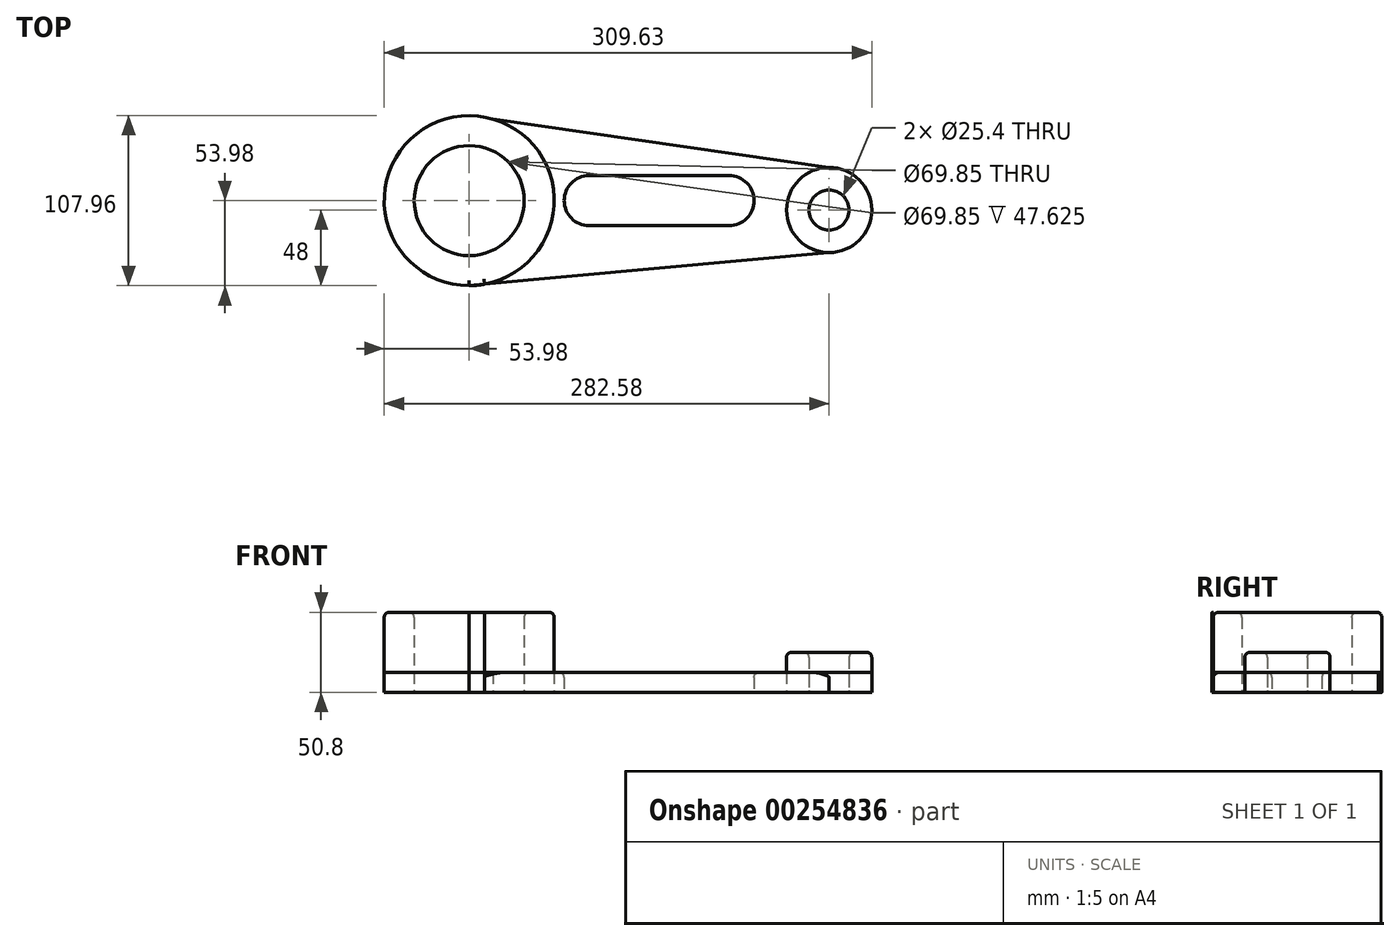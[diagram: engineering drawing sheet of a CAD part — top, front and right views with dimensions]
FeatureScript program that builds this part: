
annotation { "Feature Type Name" : "Feature", "Feature Type Description" : "" }
export const myFeature = defineFeature(function(context is Context, id is Id, definition is map)
    precondition{}
    {
        {
            var Q0;
            Q0=qCreatedBy(makeId("Top.planeOp"),FACE);
            var sketch = newSketch(context, id + "F0", { "sketchPlane" : qUnion([Q0])});
            skArc(sketch, "E0", {"start": v(0, -15.88) * mm, "mid": v(15.88, 0) * mm, "end": v(0, 15.88) * mm});
            skArc(sketch, "E1", {"start": v(-88.9, 15.88) * mm, "mid": v(-104.78, 0) * mm, "end": v(-88.9, -15.88) * mm});
            skCircle(sketch, "E2", {"center": v(-165.1, 0) * mm, "radius": 34.93 * mm});
            skCircle(sketch, "E3", {"center": v(-165.1, 0) * mm, "radius": 53.98 * mm});
            skCircle(sketch, "E4", {"center": v(63.5, -5.98) * mm, "radius": 12.7 * mm});
            skCircle(sketch, "E5", {"center": v(63.5, -5.98) * mm, "radius": 27.05 * mm});
            skLineSegment(sketch, "E6", {"start": v(-165.1, 53.98) * mm, "end": v(63.5, 21.07) * mm});
            skLineSegment(sketch, "E7", {"start": v(-165.1, -53.98) * mm, "end": v(63.5, -33.14) * mm});
            skLineSegment(sketch, "E8", {"start": v(-88.9, 15.88) * mm, "end": v(0, 15.88) * mm});
            skLineSegment(sketch, "E9", {"start": v(-88.9, -15.88) * mm, "end": v(0, -15.88) * mm});
            skCircle(sketch, "E10", {"center": v(-165.1, 0) * mm, "radius": 53.97 * mm});
            skPoint(sketch, "E10.third.point", {"position": v(-111.23, 3.36) * mm});
            skArc(sketch, "E11", {"start": v(-165.1, 53.97) * mm, "mid": v(-111.13, 0) * mm, "end": v(-165.1, -53.97) * mm});
            skArc(sketch, "E12", {"start": v(63.5, 21.07) * mm, "mid": v(36.45, -5.98) * mm, "end": v(63.5, -33.03) * mm});
            skLineSegment(sketch, "E13", {"start": v(-165.1, -53.98) * mm, "end": v(63.5, -33.03) * mm});
            skSolve(sketch);
        }
        {
            var Q0;
            {var subQ0=sQuery(id+"F0.wireOp",EDGE,"E10");var subQ1=sQuery(id+"F0.wireOp",EDGE,"E6");var subQ2=makeQuery(id+"F0.imprint","INTERSECT",VERTEX,{"disambiguationData":[OD(0.0)],"derivedFrom":[subQ1,subQ0]});Q0=makeQuery(id+"F0.imprint","IMPRINT",FACE,{"disambiguationData":[TD([[makeQuery(id+"F0.imprint","IMPRINT",EDGE,{"disambiguationData":[TD([[subQ2,-1.0]])],"derivedFrom":subQ1}),1.0]])]});}
            var Q1;
            {var subQ0=sQuery(id+"F0.wireOp",EDGE,"E10");var subQ1=sQuery(id+"F0.wireOp",EDGE,"E7");var subQ2=makeQuery(id+"F0.imprint","INTERSECT",VERTEX,{"disambiguationData":[OD(0.0)],"derivedFrom":[subQ1,subQ0]});Q1=makeQuery(id+"F0.imprint","IMPRINT",FACE,{"disambiguationData":[TD([[makeQuery(id+"F0.imprint","IMPRINT",EDGE,{"disambiguationData":[TD([[subQ2,-1.0]])],"derivedFrom":subQ1}),-1.0]])]});}
            var Q2;
            Q2=makeQuery(id+"F0.imprint","IMPRINT",FACE,{"disambiguationData":[TD([[makeQuery(id+"F0.imprint","IMPRINT",EDGE,{"derivedFrom":sQuery(id+"F0.wireOp",EDGE,"E2")}),-1.0]])]});
            extrude(context, id + "F1", {"entities" : qUnion([Q0, Q1, Q2]), "depth" : 50.8 * mm});
        }
        {
            var Q0;
            Q0=makeQuery(id+"F0.imprint","IMPRINT",FACE,{"disambiguationData":[TD([[makeQuery(id+"F0.imprint","IMPRINT",EDGE,{"derivedFrom":sQuery(id+"F0.wireOp",EDGE,"E4")}),-1.0]])]});
            extrude(context, id + "F2", {"entities" : qUnion([Q0]), "depth" : 25.4 * mm});
        }
        {
            var Q0;
            Q0 = qSketchRegion(id + "F0", true);
            extrude(context, id + "F3", {"entities" : qUnion([Q0]), "depth" : 12.7 * mm});
        }
        {
            var Q0;
            {var subQ0=sQuery(id+"F0.wireOp",EDGE,"E10");Q0=makeQuery(id+"F1.opExtrude","CAP_EDGE",EDGE,{"disambiguationData":[OSD([subQ0]),TDD([makeQuery(id+"F0.imprint","IMPRINT",EDGE,{"disambiguationData":[TD([[makeQuery(id+"F0.imprint","INTERSECT",VERTEX,{"disambiguationData":[OD(0.0)],"derivedFrom":[subQ0,sQuery(id+"F0.wireOp",EDGE,"E6")]}),-1.0]])],"derivedFrom":subQ0})])],"isStart":false});}
            var Q1;
            Q1=makeQuery(id+"F1.opExtrude","CAP_EDGE",EDGE,{"disambiguationData":[OSD([sQuery(id+"F0.wireOp",EDGE,"E13")])],"isStart":false});
            var Q2;
            {var subQ0=sQuery(id+"F0.wireOp",EDGE,"E10");Q2=makeQuery(id+"F1.opExtrude","CAP_EDGE",EDGE,{"disambiguationData":[OSD([subQ0]),TDD([makeQuery(id+"F0.imprint","IMPRINT",EDGE,{"disambiguationData":[TD([[makeQuery(id+"F0.imprint","INTERSECT",VERTEX,{"disambiguationData":[OD(1.0)],"derivedFrom":[subQ0,sQuery(id+"F0.wireOp",EDGE,"E6")]}),1.0]])],"derivedFrom":subQ0})])],"isStart":false});}
            var Q3;
            Q3=makeQuery(id+"F1.opExtrude","CAP_EDGE",EDGE,{"disambiguationData":[OSD([sQuery(id+"F0.wireOp",EDGE,"E6")])],"isStart":false});
            var Q4;
            Q4=makeQuery(id+"F1.opExtrude","CAP_FACE",FACE,{"disambiguationData":[OSD([sQuery(id+"F0.wireOp",EDGE,"E2"),sQuery(id+"F0.wireOp",EDGE,"E10"),sQuery(id+"F0.wireOp",EDGE,"E6"),sQuery(id+"F0.wireOp",EDGE,"E13")])],"isStart":false});
            var Q5;
            Q5=makeQuery(id+"F2.opExtrude","CAP_EDGE",EDGE,{"disambiguationData":[OSD([sQuery(id+"F0.wireOp",EDGE,"E5")])],"isStart":false});
            var Q6;
            Q6=makeQuery(id+"F2.opExtrude","CAP_EDGE",EDGE,{"disambiguationData":[OSD([sQuery(id+"F0.wireOp",EDGE,"E4")])],"isStart":false});
            var Q7;
            Q7=makeQuery(id+"F3.opExtrude","CAP_EDGE",EDGE,{"disambiguationData":[OSD([sQuery(id+"F0.wireOp",EDGE,"E13")])],"isStart":false});
            var Q8;
            Q8=makeQuery(id+"F3.opExtrude","CAP_EDGE",EDGE,{"disambiguationData":[OSD([sQuery(id+"F0.wireOp",EDGE,"E9")])],"isStart":false});
            var Q9;
            Q9=makeQuery(id+"F3.opExtrude","CAP_EDGE",EDGE,{"disambiguationData":[OSD([sQuery(id+"F0.wireOp",EDGE,"E1")])],"isStart":false});
            var Q10;
            Q10=makeQuery(id+"F3.opExtrude","CAP_EDGE",EDGE,{"disambiguationData":[OSD([sQuery(id+"F0.wireOp",EDGE,"E8")])],"isStart":false});
            var Q11;
            Q11=makeQuery(id+"F3.opExtrude","CAP_EDGE",EDGE,{"disambiguationData":[OSD([sQuery(id+"F0.wireOp",EDGE,"E0")])],"isStart":false});
            var Q12;
            Q12=makeQuery(id+"F3.opExtrude","CAP_EDGE",EDGE,{"disambiguationData":[OSD([sQuery(id+"F0.wireOp",EDGE,"E6")])],"isStart":false});
            fillet(context, id + "F4", {"entities" : qUnion([Q0, Q1, Q2, Q3, Q4, Q5, Q6, Q7, Q8, Q9, Q10, Q11, Q12]), "radius" : 3.17 * mm, "tangentPropagation" : true, "allowEdgeOverflow" : false});
        }
    });
